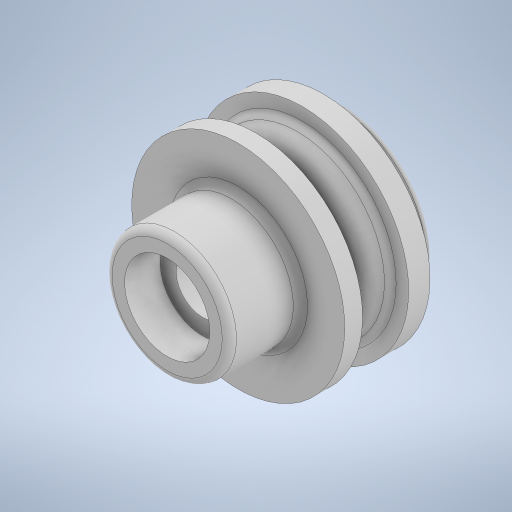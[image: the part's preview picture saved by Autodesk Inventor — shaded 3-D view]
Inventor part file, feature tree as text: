
AUTODESK INVENTOR PART (.ipt)
format: ipt  version: 2023 (Build 270158000, 158)  size: 376,832 bytes
history: native  units: mm
features: revolve x1, fillet x1, sketch x1
ambient origin geometry x8: Origin, YZ Plane, XZ Plane, XY Plane, X Axis, Y Axis, Z Axis, Center Point
bodies: Solido1 (feature_tree)
feature tree (3):
  revolve  "Rivoluzione1"
  fillet  "Raccordo1"  Radius=15.0mm
  sketch  "Schizzo1"
